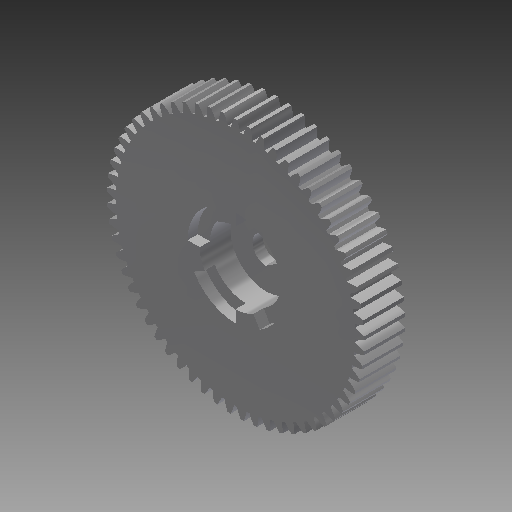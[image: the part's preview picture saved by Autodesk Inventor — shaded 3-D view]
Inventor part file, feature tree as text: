
AUTODESK INVENTOR PART (.ipt)
format: ipt  version: 2017 (Build 210142000, 142)  size: 443,904 bytes
history: native  units: mm (DEFAULTED — no unit token found)
features: sketch x5, extrude x4, plane x3, other x3, pattern_circular x1
ambient origin geometry x8: Origin, YZ Plane, XZ Plane, XY Plane, X Axis, Y Axis, Z Axis, Center Point
bodies: Solid1 (feature_tree)
feature tree (16):
  extrude  "Extrusion1"  Depth=20.0mm TaperAngle=0.0deg
  plane  "Work Plane2"
  plane  "Work Plane8"
  plane  "Work Plane9"
  other  "Spur Gear"
  extrude  "Extrusion2"  Depth=10.0mm TaperAngle=0.0deg
  extrude  "Extrusion3"  Depth=0.515015mm TaperAngle=0.0deg
  extrude  "Extrusion4"  TaperAngle=0.0deg  [1 undecoded]
  pattern_circular  "Circular Pattern1"  Count=8  [1 undecoded]
  sketch  "Sketch1"  dims[d0=126.0mm d1=20.0mm d2=0.0mm]
  sketch  "Sketch2"  dims[d3=122.0mm d4=10.0mm d5=0.0mm]
  other  "Srf1"
  sketch  "Sketch3"  dims[d16=80.0mm d17=0.0mm d34=0.515015mm]
  sketch  "Sketch4"  dims[d39=0.0mm d41=0.0mm d43=80.0mm]
  sketch  "Sketch5"  dims[d46=80.0mm d47=0.0mm d48=0.0mm d49=9.525mm d50=10.0mm d51=0.0mm d52=35.0mm d53=15.0mm d54=0.0mm d55=6.0mm d56=60.0deg d57=5.0mm d58=0.0mm d59=40.0mm d60=360.0deg]
  other  "Pitch Diameter"
note: 2 required parameter values undecoded (feature->parameter linkage not recoverable at this tier; creation-order binding heuristic only, values carry confidence <= 0.55)
